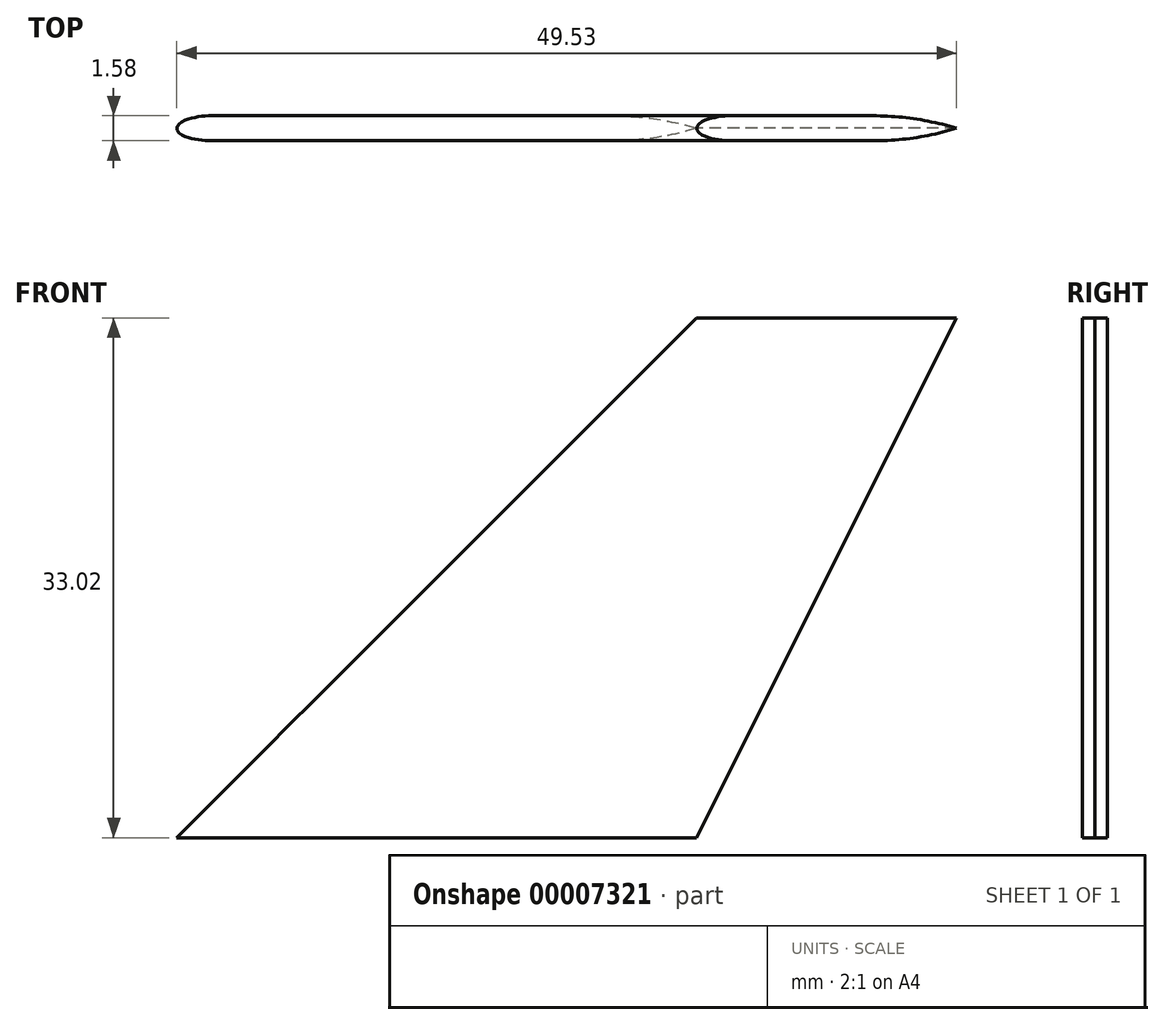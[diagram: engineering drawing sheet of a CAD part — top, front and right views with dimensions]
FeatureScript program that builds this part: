
annotation { "Feature Type Name" : "Feature", "Feature Type Description" : "" }
export const myFeature = defineFeature(function(context is Context, id is Id, definition is map)
    precondition{}
    {
        {
            var Q0;
            Q0=qCreatedBy(makeId("Front.planeOp"),FACE);
            var sketch = newSketch(context, id + "F0", { "sketchPlane" : qUnion([Q0])});
            skLineSegment(sketch, "E0", {"start": v(0, 0) * mm, "end": v(33.02, 33.02) * mm});
            skLineSegment(sketch, "E1", {"start": v(33.02, 33.02) * mm, "end": v(49.53, 33.02) * mm});
            skLineSegment(sketch, "E2", {"start": v(49.53, 33.02) * mm, "end": v(33.02, 0) * mm});
            skLineSegment(sketch, "E3", {"start": v(33.02, 0) * mm, "end": v(0, 0) * mm});
            skSolve(sketch);
        }
        {
            var Q0;
            Q0=makeQuery(id+"F0.imprint","IMPRINT",FACE,{"disambiguationData":[TD([[makeQuery(id+"F0.imprint","IMPRINT",EDGE,{"derivedFrom":sQuery(id+"F0.wireOp",EDGE,"E0")}),-1.0]])]});
            extrude(context, id + "F1", {"entities" : qUnion([Q0]), "depth" : 1.59 * mm, "symmetric" : true});
        }
        {
            var Q0;
            Q0=sQuery(id+"F0.wireOp",EDGE,"E0");
            var Q1;
            Q1=sQuery(id+"F0.wireOp",VERTEX,"E3.end");
            cPlane(context, id + "F2", {"entities" : qUnion([Q0, Q1]), "cplaneType" : CPlaneType.CURVE_POINT, "offset" : 152.4 * mm, "width" : 152.4 * mm, "height" : 152.4 * mm});
        }
        {
            var Q0;
            Q0=qCreatedBy(id+"F2.planeOp",FACE);
            var sketch = newSketch(context, id + "F3", { "sketchPlane" : qUnion([Q0])});
            skLineSegment(sketch, "E4.0", {"start": v(0.8, 0) * mm, "end": v(0.8, -11.67) * mm, "construction": true});
            skLineSegment(sketch, "E4.1", {"start": v(-0.8, 0) * mm, "end": v(-0.8, -11.67) * mm, "construction": true});
            skLineSegment(sketch, "E4.2", {"start": v(-0.8, 0) * mm, "end": v(0.8, 0) * mm, "construction": true});
            skLineSegment(sketch, "E5.0", {"start": v(0, -23.35) * mm, "end": v(0, 0) * mm, "construction": true});
            skCircle(sketch, "E6", {"center": v(0, -0.8) * mm, "radius": 0.8 * mm, "construction": true});
            skLineSegment(sketch, "E7", {"start": v(0.8, -1.59) * mm, "end": v(-0.8, -1.59) * mm});
            skEllipticalArc(sketch, "E8", {});
            skLineSegment(sketch, "E9", {"start": v(3.33, 2.54) * mm, "end": v(-3.33, 2.54) * mm});
            skLineSegment(sketch, "E10", {"start": v(-3.33, 2.54) * mm, "end": v(-3.33, -1.59) * mm});
            skLineSegment(sketch, "E11", {"start": v(-3.33, -1.59) * mm, "end": v(-0.8, -1.59) * mm});
            skLineSegment(sketch, "E12", {"start": v(3.33, 2.54) * mm, "end": v(3.33, -1.59) * mm});
            skLineSegment(sketch, "E13", {"start": v(3.33, -1.59) * mm, "end": v(0.8, -1.59) * mm});
            const initialGuessF3  = {"E8": [0, -0.001587500000000002, 0, 1, 0.0015874999999999978, 0.0007937500000000001, 4.71238898038469, 1.5707963267948966]};
            skSetInitialGuess(sketch, initialGuessF3);
            skSolve(sketch);
        }
        {
            var Q0;
            Q0=makeQuery(id+"F3.imprint","IMPRINT",FACE,{"disambiguationData":[TD([[makeQuery(id+"F3.imprint","IMPRINT",EDGE,{"derivedFrom":sQuery(id+"F3.wireOp",EDGE,"E8")}),-1.0]])]});
            extrude(context, id + "F4", {"entities" : qUnion([Q0]), "operationType" : NewBodyOperationType.REMOVE, "endBound" : BoundingType.THROUGH_ALL, "depth" : 25.4 * mm});
        }
        {
            var Q0;
            Q0=sQuery(id+"F0.wireOp",EDGE,"E2");
            var Q1;
            Q1=sQuery(id+"F0.wireOp",VERTEX,"E3.start");
            cPlane(context, id + "F5", {"entities" : qUnion([Q0, Q1]), "cplaneType" : CPlaneType.CURVE_POINT, "offset" : 152.4 * mm, "width" : 152.4 * mm, "height" : 152.4 * mm});
        }
        {
            var Q0;
            Q0=qCreatedBy(id+"F5.planeOp",FACE);
            var sketch = newSketch(context, id + "F6", { "sketchPlane" : qUnion([Q0])});
            skLineSegment(sketch, "E14.0", {"start": v(26.36, -0.8) * mm, "end": v(29.53, -0.8) * mm, "construction": true});
            skLineSegment(sketch, "E14.1", {"start": v(29.53, 0.8) * mm, "end": v(29.53, -0.8) * mm, "construction": true});
            skLineSegment(sketch, "E14.2", {"start": v(26.36, 0.8) * mm, "end": v(29.53, 0.8) * mm, "construction": true});
            skLineSegment(sketch, "E14.3", {"start": v(29.53, 0) * mm, "end": v(0, 0) * mm, "construction": true});
            skCircle(sketch, "E15", {"center": v(28.74, 0) * mm, "radius": 0.8 * mm, "construction": true});
            skCircle(sketch, "E16", {"center": v(27.15, 0) * mm, "radius": 0.8 * mm, "construction": true});
            skLineSegment(sketch, "E17", {"start": v(26.36, -0.8) * mm, "end": v(26.36, 0.8) * mm, "construction": true});
            skLineSegment(sketch, "E18", {"start": v(26.36, -0.8) * mm, "end": v(24.77, -0.8) * mm, "construction": true});
            skPoint(sketch, "E18.endSnap0", {"position": v(14.77, 0) * mm});
            skArc(sketch, "E19", {"start": v(26.36, -0.8) * mm, "mid": v(28, -0.6) * mm, "end": v(29.53, 0) * mm, "construction": true});
            skCircle(sketch, "E20", {"center": v(25.57, 0) * mm, "radius": 0.8 * mm, "construction": true});
            skLineSegment(sketch, "E21", {"start": v(26.36, 0.8) * mm, "end": v(14.77, 0.8) * mm, "construction": true});
            skLineSegment(sketch, "E22", {"start": v(24.77, -0.8) * mm, "end": v(24.77, 0.8) * mm, "construction": true});
            skLineSegment(sketch, "E23", {"start": v(24.77, -0.8) * mm, "end": v(14.77, -0.8) * mm});
            skLineSegment(sketch, "E24", {"start": v(14.77, -0.8) * mm, "end": v(14.77, 0.8) * mm});
            skArc(sketch, "E25", {"start": v(24.77, -0.8) * mm, "mid": v(27.19, -0.6) * mm, "end": v(29.53, 0) * mm});
            skLineSegment(sketch, "E26", {"start": v(24.77, -0.8) * mm, "end": v(24.77, -3.33) * mm});
            skLineSegment(sketch, "E27", {"start": v(24.77, -3.33) * mm, "end": v(32.07, -3.33) * mm});
            skLineSegment(sketch, "E28", {"start": v(32.07, -3.33) * mm, "end": v(32.07, 3.33) * mm});
            skLineSegment(sketch, "E29", {"start": v(32.07, 3.33) * mm, "end": v(24.77, 3.33) * mm});
            skLineSegment(sketch, "E30", {"start": v(24.77, 3.33) * mm, "end": v(24.77, 0.8) * mm});
            skArc(sketch, "E31.MirrorCS", {"start": v(24.77, 0.8) * mm, "mid": v(27.19, 0.6) * mm, "end": v(29.53, 0) * mm});
            skSolve(sketch);
        }
        {
            var Q0;
            Q0=makeQuery(id+"F6.imprint","IMPRINT",FACE,{"disambiguationData":[TD([[makeQuery(id+"F6.imprint","IMPRINT",EDGE,{"derivedFrom":sQuery(id+"F6.wireOp",EDGE,"E25")}),-1.0]])]});
            extrude(context, id + "F7", {"entities" : qUnion([Q0]), "operationType" : NewBodyOperationType.REMOVE, "oppositeDirection" : true, "depth" : 127 * mm, "symmetric" : true});
        }
    });
